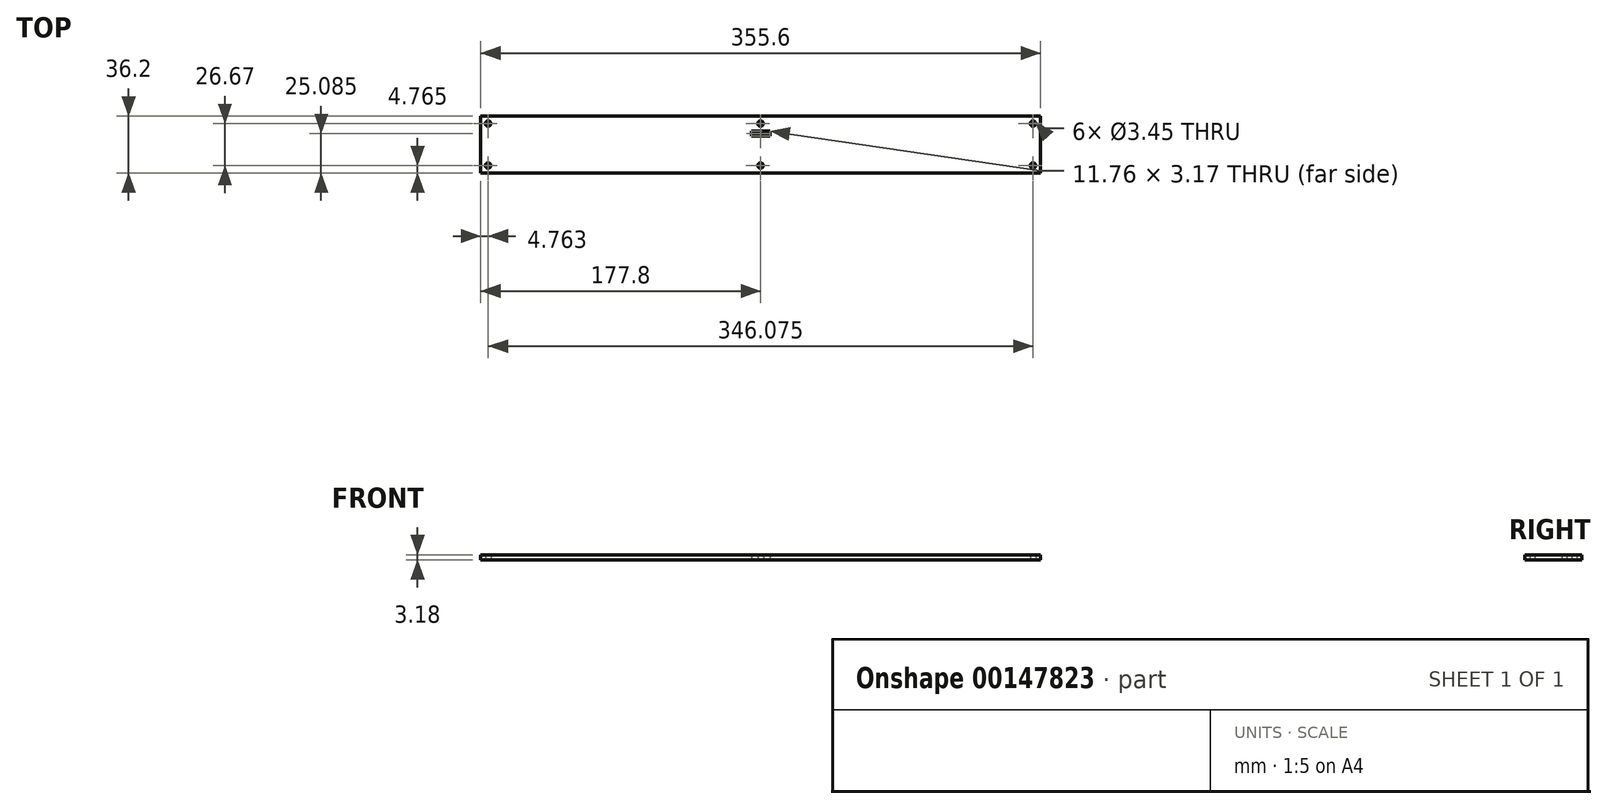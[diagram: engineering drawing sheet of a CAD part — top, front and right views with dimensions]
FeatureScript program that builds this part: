
annotation { "Feature Type Name" : "Feature", "Feature Type Description" : "" }
export const myFeature = defineFeature(function(context is Context, id is Id, definition is map)
    precondition{}
    {
        {
            var Q0;
            Q0=qCreatedBy(makeId("Top.planeOp"),FACE);
            var sketch = newSketch(context, id + "F0", { "sketchPlane" : qUnion([Q0])});
            skLineSegment(sketch, "E0.bottom", {"start": v(177.8, -18.1) * mm, "end": v(-177.8, -18.1) * mm});
            skLineSegment(sketch, "E0.top", {"start": v(177.8, 18.1) * mm, "end": v(-177.8, 18.1) * mm});
            skLineSegment(sketch, "E0.left", {"start": v(177.8, -18.1) * mm, "end": v(177.8, 18.1) * mm});
            skLineSegment(sketch, "E0.right", {"start": v(-177.8, -18.1) * mm, "end": v(-177.8, 18.1) * mm});
            skPoint(sketch, "E0.middle", {"position": v(0, 0) * mm});
            skLineSegment(sketch, "E1.bottom", {"start": v(173.04, -13.33) * mm, "end": v(-173.04, -13.34) * mm, "construction": true});
            skLineSegment(sketch, "E1.top", {"start": v(173.04, 13.34) * mm, "end": v(-173.04, 13.34) * mm, "construction": true});
            skLineSegment(sketch, "E1.left", {"start": v(173.04, -13.34) * mm, "end": v(173.04, 13.34) * mm, "construction": true});
            skLineSegment(sketch, "E1.right", {"start": v(-173.04, -13.34) * mm, "end": v(-173.04, 13.34) * mm, "construction": true});
            skLineSegment(sketch, "E2", {"start": v(-173.04, -13.34) * mm, "end": v(-173.04, -18.1) * mm, "construction": true});
            skLineSegment(sketch, "E3", {"start": v(-173.04, -13.34) * mm, "end": v(-177.8, -13.34) * mm, "construction": true});
            skCircle(sketch, "E4", {"center": v(-173.04, 13.34) * mm, "radius": 1.73 * mm});
            skCircle(sketch, "E5", {"center": v(-173.04, -13.34) * mm, "radius": 1.73 * mm});
            skCircle(sketch, "E6", {"center": v(173.04, -13.34) * mm, "radius": 1.73 * mm});
            skCircle(sketch, "E7", {"center": v(173.04, 13.34) * mm, "radius": 1.73 * mm});
            skCircle(sketch, "E8", {"center": v(0, 13.34) * mm, "radius": 1.73 * mm});
            skCircle(sketch, "E9", {"center": v(0, -13.34) * mm, "radius": 1.73 * mm});
            skLineSegment(sketch, "E10", {"start": v(0, -13.34) * mm, "end": v(0, 6.99) * mm, "construction": true});
            skLineSegment(sketch, "E11.bottom", {"start": v(-5.88, 5.4) * mm, "end": v(5.88, 5.4) * mm});
            skLineSegment(sketch, "E11.top", {"start": v(-5.88, 8.57) * mm, "end": v(5.88, 8.57) * mm});
            skLineSegment(sketch, "E11.left", {"start": v(-5.88, 5.4) * mm, "end": v(-5.88, 8.57) * mm});
            skLineSegment(sketch, "E11.right", {"start": v(5.88, 5.4) * mm, "end": v(5.88, 8.57) * mm});
            skLineSegment(sketch, "E12", {"start": v(-5.88, 6.99) * mm, "end": v(5.88, 6.99) * mm, "construction": true});
            skLineSegment(sketch, "E13", {"start": v(0, 8.57) * mm, "end": v(0, 13.34) * mm, "construction": true});
            skSolve(sketch);
        }
        {
            var Q0;
            Q0=qSketchRegion(id+"F0",true);
            extrude(context, id + "F1", {"entities" : qUnion([Q0]), "depth" : 3.17 * mm});
        }
    });
